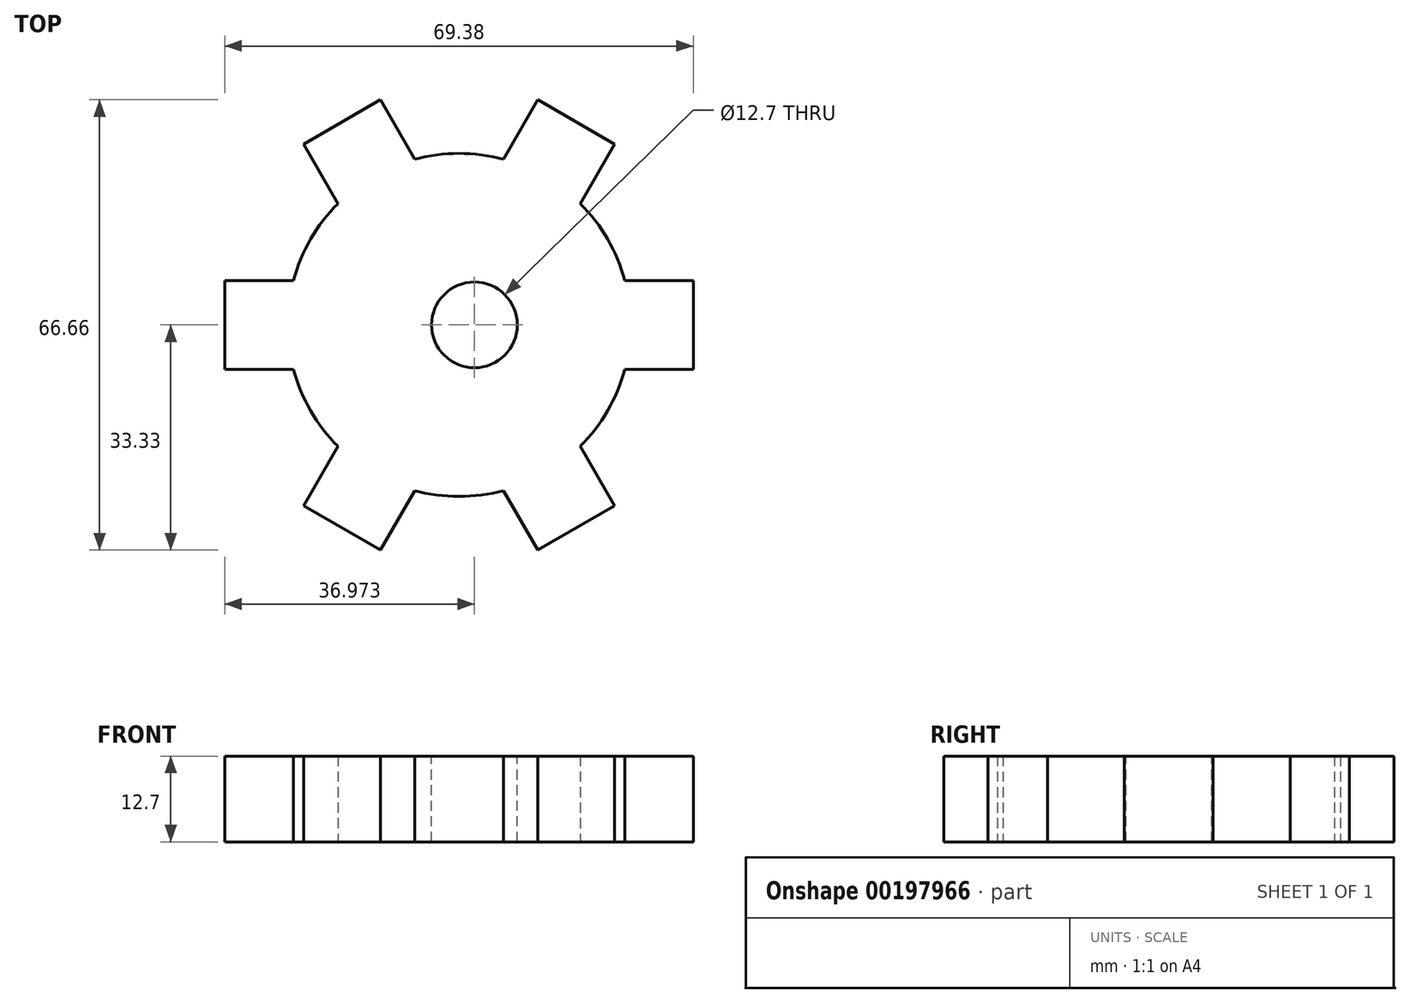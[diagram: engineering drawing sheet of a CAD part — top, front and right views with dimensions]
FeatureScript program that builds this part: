
annotation { "Feature Type Name" : "Feature", "Feature Type Description" : "" }
export const myFeature = defineFeature(function(context is Context, id is Id, definition is map)
    precondition{}
    {
        {
            var Q0;
            Q0=qCreatedBy(makeId("Top.planeOp"),FACE);
            var sketch = newSketch(context, id + "F0", { "sketchPlane" : qUnion([Q0])});
            skCircle(sketch, "E0", {"center": v(0, 0) * mm, "radius": 25.4 * mm});
            skSolve(sketch);
        }
        {
            var Q0;
            Q0 = qSketchRegion(id + "F0", true);
            extrude(context, id + "F1", {"entities" : qUnion([Q0]), "depth" : 12.7 * mm});
        }
        {
            var Q0;
            Q0=makeQuery(id+"F1.opExtrude","CAP_FACE",FACE,{"disambiguationData":[OSD([sQuery(id+"F0.wireOp",EDGE,"E0")])],"isStart":true});
            var sketch = newSketch(context, id + "F2", { "sketchPlane" : qUnion([Q0])});
            skLineSegment(sketch, "E1", {"start": v(0, 0) * mm, "end": v(25.4, 0) * mm});
            skPoint(sketch, "E2.orphan", {"position": v(7.59, -17.26) * mm});
            skPoint(sketch, "E3.end.orphan", {"position": v(16.5, -8.63) * mm});
            skLineSegment(sketch, "E4", {"start": v(0, 0) * mm, "end": v(24.53, 6.57) * mm});
            skLineSegment(sketch, "E5", {"start": v(0, 0) * mm, "end": v(24.53, -6.57) * mm});
            skLineSegment(sketch, "E6", {"start": v(24.53, 6.57) * mm, "end": v(24.53, -6.57) * mm});
            skLineSegment(sketch, "E7.0", {"start": v(34.7, 6.57) * mm, "end": v(34.7, -6.57) * mm});
            skLineSegment(sketch, "E8", {"start": v(34.7, 6.57) * mm, "end": v(24.53, 6.57) * mm});
            skLineSegment(sketch, "E9", {"start": v(34.7, -6.57) * mm, "end": v(24.53, -6.57) * mm});
            skSolve(sketch);
        }
        {
            var Q0;
            Q0 = qSketchRegion(id + "F2", true);
            extrude(context, id + "F3", {"entities" : qUnion([Q0]), "operationType" : NewBodyOperationType.ADD, "oppositeDirection" : true, "depth" : 12.7 * mm});
        }
        {
            var Q0;
            Q0=qCreatedBy(makeId("Front.planeOp"),FACE);
            var sketch = newSketch(context, id + "F4", { "sketchPlane" : qUnion([Q0])});
            skLineSegment(sketch, "E10", {"start": v(0, -2.4) * mm, "end": v(0, 0) * mm});
            skLineSegment(sketch, "E11", {"start": v(0, 0) * mm, "end": v(0, 45.05) * mm});
            skSolve(sketch);
        }
        {
            var Q0;
            Q0=makeQuery(id+"F1.opExtrude","SWEPT_BODY",BODY,{"disambiguationData":[OSD([sQuery(id+"F0.wireOp",EDGE,"E0")])]});
            var Q1;
            Q1=sQuery(id+"F4.wireOp",EDGE,"E11");
            circularPattern(context, id + "F5", {"operationType" : NewBodyOperationType.ADD, "entities" : qUnion([Q0]), "axis" : qUnion([Q1]), "angle" : 360 * degree, "instanceCount" : 6, "equalSpace" : true});
        }
        {
            var Q0;
            {var subQ0=makeQuery(id+"F3.boolean.opBoolean","MERGE",FACE,{"derivedFrom":[makeQuery(id+"F1.opExtrude","CAP_FACE",FACE,{"disambiguationData":[OSD([sQuery(id+"F0.wireOp",EDGE,"E0")])],"isStart":false}),makeQuery(id+"F3.opExtrude","CAP_FACE",FACE,{"disambiguationData":[OSD([sQuery(id+"F2.wireOp",EDGE,"E4"),sQuery(id+"F2.wireOp",EDGE,"E5"),sQuery(id+"F2.wireOp",EDGE,"E7.0"),sQuery(id+"F2.wireOp",EDGE,"E8"),sQuery(id+"F2.wireOp",EDGE,"E9")])],"isStart":false})]});Q0=makeQuery(id+"F5.boolean.opBoolean","MERGE",FACE,{"derivedFrom":[subQ0,makeQuery(id+"F5.opPattern","COPY",FACE,{"derivedFrom":subQ0,"instanceName":"1"}),makeQuery(id+"F5.opPattern","COPY",FACE,{"derivedFrom":subQ0,"instanceName":"2"}),makeQuery(id+"F5.opPattern","COPY",FACE,{"derivedFrom":subQ0,"instanceName":"3"}),makeQuery(id+"F5.opPattern","COPY",FACE,{"derivedFrom":subQ0,"instanceName":"4"}),makeQuery(id+"F5.opPattern","COPY",FACE,{"derivedFrom":subQ0,"instanceName":"5"})]});}
            var sketch = newSketch(context, id + "F6", { "sketchPlane" : qUnion([Q0])});
            skPoint(sketch, "E12.center.orphan", {"position": v(0, 0) * mm});
            skCircle(sketch, "E13", {"center": v(2.28, 0) * mm, "radius": 6.35 * mm});
            skSolve(sketch);
        }
        {
            var Q0;
            Q0=makeQuery(id+"F6.imprint","IMPRINT",FACE,{"disambiguationData":[TD([[makeQuery(id+"F6.imprint","IMPRINT",EDGE,{"derivedFrom":sQuery(id+"F6.wireOp",EDGE,"E13")}),1.0]])]});
            extrude(context, id + "F7", {"entities" : qUnion([Q0]), "operationType" : NewBodyOperationType.REMOVE, "oppositeDirection" : true, "depth" : 25.4 * mm});
        }
    });
